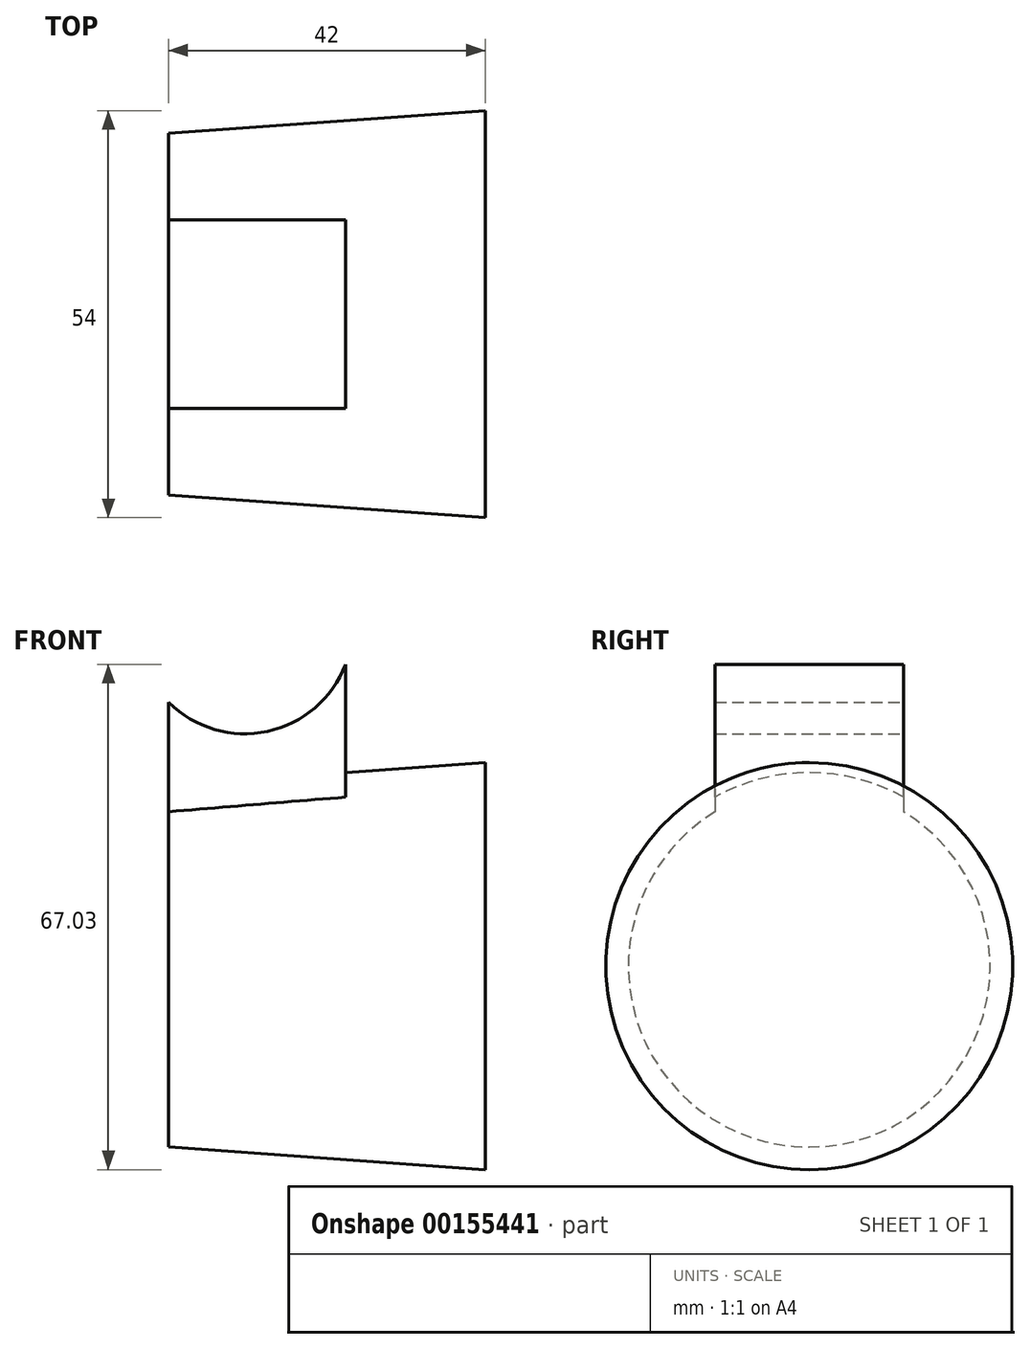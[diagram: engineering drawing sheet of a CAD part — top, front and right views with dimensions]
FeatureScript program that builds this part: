
annotation { "Feature Type Name" : "Feature", "Feature Type Description" : "" }
export const myFeature = defineFeature(function(context is Context, id is Id, definition is map)
    precondition{}
    {
        {
            var Q0;
            Q0=qCreatedBy(makeId("Front.planeOp"),FACE);
            var sketch = newSketch(context, id + "F0", { "sketchPlane" : qUnion([Q0])});
            skLineSegment(sketch, "E0", {"start": v(0, 27) * mm, "end": v(-42, 24) * mm});
            skLineSegment(sketch, "E1", {"start": v(-42, 24) * mm, "end": v(-42, 0) * mm});
            skLineSegment(sketch, "E2", {"start": v(-42, 0) * mm, "end": v(0, 0) * mm});
            skLineSegment(sketch, "E3", {"start": v(0, 0) * mm, "end": v(0, 27) * mm});
            skSolve(sketch);
        }
        {
            var Q0;
            Q0 = qSketchRegion(id + "F0", true);
            var Q1;
            Q1=sQuery(id+"F0.wireOp",EDGE,"E2");
            revolve(context, id + "F1", {"entities" : qUnion([Q0]), "axis" : qUnion([Q1]), "revolveType" : RevolveType.FULL});
        }
        {
            var Q0;
            Q0=qCreatedBy(makeId("Front.planeOp"),FACE);
            var sketch = newSketch(context, id + "F2", { "sketchPlane" : qUnion([Q0])});
            skLineSegment(sketch, "E4", {"start": v(-42, 35) * mm, "end": v(0, 44) * mm, "construction": true});
            skLineSegment(sketch, "E5", {"start": v(0, -27) * mm, "end": v(-42, -24) * mm, "construction": true});
            skLineSegment(sketch, "E6", {"start": v(-42, 24) * mm, "end": v(0, 27) * mm, "construction": true});
            skLineSegment(sketch, "E7.0.0", {"start": v(0, 27) * mm, "end": v(0, -27) * mm, "construction": true});
            skLineSegment(sketch, "E8.0.0", {"start": v(-42, -24) * mm, "end": v(-42, 24) * mm, "construction": true});
            skArc(sketch, "E9", {"start": v(-42, 35) * mm, "mid": v(-28.9, 31.16) * mm, "end": v(-18.53, 40.03) * mm});
            skLineSegment(sketch, "E10", {"start": v(-42, 35) * mm, "end": v(-42, 0) * mm});
            skLineSegment(sketch, "E11", {"start": v(-42, 0) * mm, "end": v(-18.53, 0) * mm});
            skLineSegment(sketch, "E12", {"start": v(-18.53, 0) * mm, "end": v(-18.53, 40.03) * mm});
            skSolve(sketch);
        }
        {
            var Q0;
            Q0 = qSketchRegion(id + "F2", true);
            extrude(context, id + "F3", {"entities" : qUnion([Q0]), "operationType" : NewBodyOperationType.ADD, "endBound" : BoundingType.SYMMETRIC, "depth" : 25 * mm});
        }
    });
